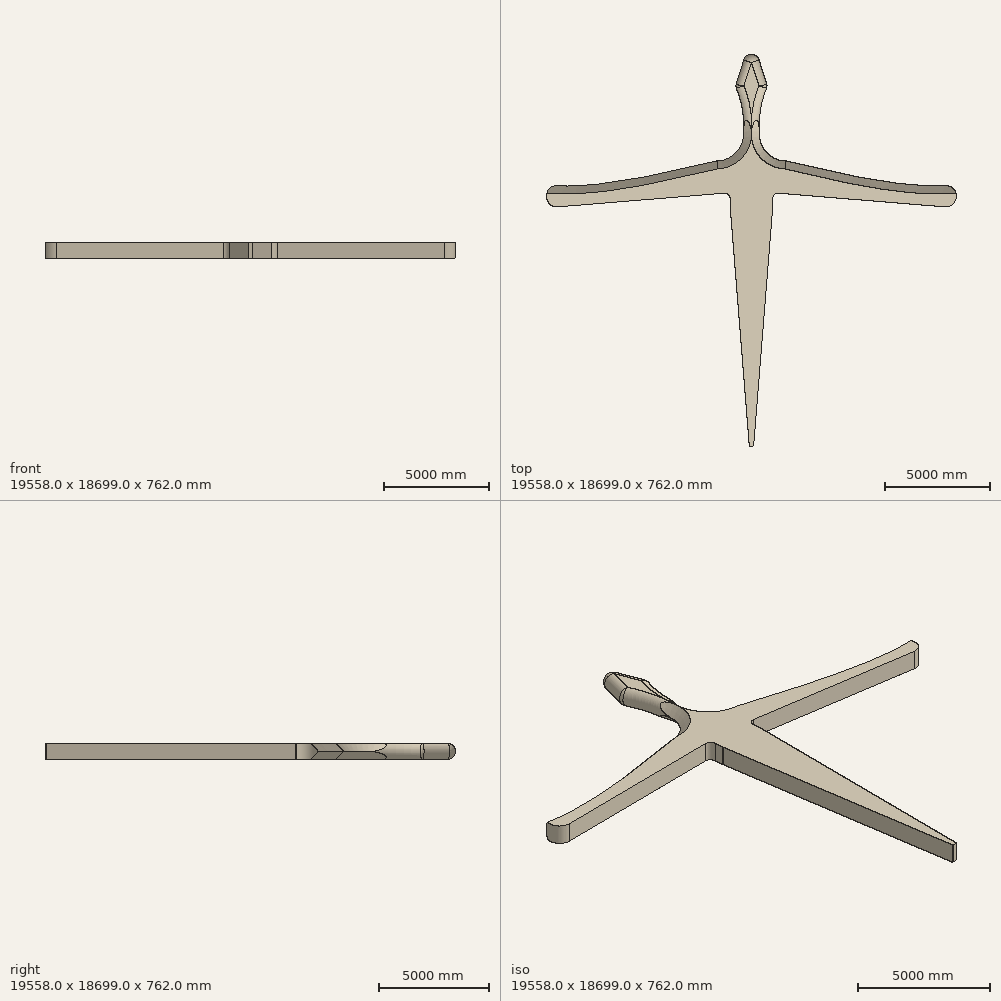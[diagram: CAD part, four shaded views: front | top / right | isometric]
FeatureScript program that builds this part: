
annotation { "Feature Type Name" : "Feature", "Feature Type Description" : "" }
export const myFeature = defineFeature(function(context is Context, id is Id, definition is map)
    precondition{}
    {
        {
            var Q0;
            Q0=qCreatedBy(makeId("Top.planeOp"),FACE);
            var sketch = newSketch(context, id + "F0", { "sketchPlane" : qUnion([Q0])});
            skArc(sketch, "E0", {"start": v(363.19, 1258.13) * mm, "mid": v(0, 1524) * mm, "end": v(-363.19, 1258.13) * mm});
            skLineSegment(sketch, "E1", {"start": v(-733.66, 89.4) * mm, "end": v(-363.19, 1258.13) * mm});
            skLineSegment(sketch, "E2", {"start": v(733.66, 89.4) * mm, "end": v(363.19, 1258.13) * mm});
            skPoint(sketch, "E3.end.orphan", {"position": v(0, 762) * mm});
            skArc(sketch, "E4", {"start": v(-381, -2286) * mm, "mid": v(-423.5, -1164.66) * mm, "end": v(-726.36, -84.15) * mm});
            skArc(sketch, "E5", {"start": v(726.36, -84.15) * mm, "mid": v(423.5, -1164.66) * mm, "end": v(381, -2286) * mm});
            skPoint(sketch, "E6.center.orphan", {"position": v(0, 0) * mm});
            skPoint(sketch, "E7.visualSharp", {"position": v(-762, 0) * mm});
            skArc(sketch, "E7.filletArc", {"start": v(-733.66, 89.4) * mm, "mid": v(-745.31, 1.98) * mm, "end": v(-726.36, -84.15) * mm});
            skPoint(sketch, "E8.visualSharp", {"position": v(762, 0) * mm});
            skArc(sketch, "E8.filletArc", {"start": v(726.36, -84.15) * mm, "mid": v(745.31, 1.98) * mm, "end": v(733.66, 89.4) * mm});
            skArc(sketch, "E9", {"start": v(-1651, -3556) * mm, "mid": v(-752.97, -3184.03) * mm, "end": v(-381, -2286) * mm});
            skArc(sketch, "E10", {"start": v(381, -2286) * mm, "mid": v(752.97, -3184.03) * mm, "end": v(1651, -3556) * mm});
            skFitSpline(sketch, "E11", {"points": [v(-1651, -3556) * mm, v(-9271, -4733.18) * mm, v(-11645.05, -3985.73) * mm], "startDerivative": vector(-13701.74, -3365.96) * mm, "endDerivative": vector(-5543.68, 3094.65) * mm});
            skFitSpline(sketch, "E12.MirrorCS", {"points": [v(1651, -3556) * mm, v(9271, -4733.18) * mm, v(11645.05, -3985.73) * mm], "startDerivative": vector(13701.74, -3365.96) * mm, "endDerivative": vector(5543.68, 3094.65) * mm});
            skArc(sketch, "E13", {"start": v(-9271, -4733.18) * mm, "mid": v(-9779, -5241.18) * mm, "end": v(-9271, -5749.18) * mm});
            skArc(sketch, "E14", {"start": v(9271, -5749.18) * mm, "mid": v(9779, -5241.18) * mm, "end": v(9271, -4733.18) * mm});
            skPoint(sketch, "E15.end.orphan", {"position": v(-9271, -5749.18) * mm});
            skLineSegment(sketch, "E16", {"start": v(-9271, -5749.18) * mm, "end": v(-1290.8, -5093.27) * mm});
            skLineSegment(sketch, "E17", {"start": v(9271, -5749.18) * mm, "end": v(1290.8, -5093.27) * mm});
            skLineSegment(sketch, "E18.bottom", {"start": v(-1016, -5749.18) * mm, "end": v(-1016, -5749.18) * mm});
            skLineSegment(sketch, "E18.top", {"start": v(-1016, -3806.69) * mm, "end": v(-1016, -3806.69) * mm});
            skLineSegment(sketch, "E18.left", {"start": v(-1016, -5749.18) * mm, "end": v(-1016, -5346.42) * mm});
            skLineSegment(sketch, "E18.right", {"start": v(-1016, -5739.04) * mm, "end": v(-1016, -5070.69) * mm});
            skLineSegment(sketch, "E19", {"start": v(1016, -5739.04) * mm, "end": v(1016, -5346.42) * mm});
            skPoint(sketch, "E20.visualSharp", {"position": v(-1016, -5070.69) * mm});
            skArc(sketch, "E20.filletArc", {"start": v(-1016, -5346.42) * mm, "mid": v(-1097.9, -5159.6) * mm, "end": v(-1290.8, -5093.27) * mm});
            skPoint(sketch, "E21.visualSharp", {"position": v(1016, -5070.69) * mm});
            skArc(sketch, "E21.filletArc", {"start": v(1290.8, -5093.27) * mm, "mid": v(1097.9, -5159.6) * mm, "end": v(1016, -5346.42) * mm});
            skLineSegment(sketch, "E22", {"start": v(-1015.2, -5759.3) * mm, "end": v(-103.92, -17150.16) * mm});
            skLineSegment(sketch, "E23", {"start": v(103.87, -17150.76) * mm, "end": v(1015.2, -5759.3) * mm});
            skPoint(sketch, "E24.visualSharp", {"position": v(-1016, -5749.18) * mm});
            skArc(sketch, "E24.filletArc", {"start": v(-1016, -5739.04) * mm, "mid": v(-1015.8, -5749.17) * mm, "end": v(-1015.2, -5759.3) * mm});
            skPoint(sketch, "E25.visualSharp", {"position": v(1016, -5749.18) * mm});
            skArc(sketch, "E25.filletArc", {"start": v(1015.2, -5759.3) * mm, "mid": v(1015.8, -5749.17) * mm, "end": v(1016, -5739.04) * mm});
            skLineSegment(sketch, "E26", {"start": v(72.12, -17174.4) * mm, "end": v(-77.67, -17174.4) * mm});
            skPoint(sketch, "E27.visualSharp", {"position": v(101.98, -17174.4) * mm});
            skArc(sketch, "E27.filletArc", {"start": v(72.12, -17174.4) * mm, "mid": v(93.35, -17169.77) * mm, "end": v(103.87, -17150.76) * mm});
            skPoint(sketch, "E28.visualSharp", {"position": v(-101.98, -17174.4) * mm});
            skArc(sketch, "E28.filletArc", {"start": v(-103.92, -17150.16) * mm, "mid": v(-95.53, -17167.41) * mm, "end": v(-77.67, -17174.4) * mm});
            skLineSegment(sketch, "E29.0", {"start": v(491.53, 12.65) * mm, "end": v(121.06, 1181.38) * mm});
            skArc(sketch, "E29.1", {"start": v(121.06, 1181.38) * mm, "mid": v(0, 1270) * mm, "end": v(-121.06, 1181.38) * mm});
            skLineSegment(sketch, "E29.2", {"start": v(-491.53, 12.65) * mm, "end": v(-121.06, 1181.38) * mm});
            skArc(sketch, "E30", {"start": v(-491.53, 12.65) * mm, "mid": v(0, -491.7) * mm, "end": v(491.53, 12.65) * mm});
            skSolve(sketch);
        }
        {
            var Q0;
            Q0=makeQuery(id+"F0.imprint","IMPRINT",FACE,{"disambiguationData":[TD([[makeQuery(id+"F0.imprint","IMPRINT",EDGE,{"derivedFrom":sQuery(id+"F0.wireOp",EDGE,"E0")}),1.0]])]});
            var Q1;
            Q1=makeQuery(id+"F0.imprint","IMPRINT",FACE,{"disambiguationData":[TD([[makeQuery(id+"F0.imprint","IMPRINT",EDGE,{"derivedFrom":sQuery(id+"F0.wireOp",EDGE,"E29.0")}),1.0]])]});
            extrude(context, id + "F1", {"entities" : qUnion([Q0, Q1]), "depth" : 762 * mm});
        }
        {
            var Q0;
            Q0=makeQuery(id+"F1.opExtrude","CAP_EDGE",EDGE,{"disambiguationData":[OSD([sQuery(id+"F0.wireOp",EDGE,"E11")])],"isStart":false});
            var Q1;
            Q1=makeQuery(id+"F1.opExtrude","CAP_EDGE",EDGE,{"disambiguationData":[OSD([sQuery(id+"F0.wireOp",EDGE,"E12.MirrorCS")])],"isStart":false});
            var Q2;
            Q2=makeQuery(id+"F1.opExtrude","CAP_EDGE",EDGE,{"disambiguationData":[OSD([sQuery(id+"F0.wireOp",EDGE,"E10")])],"isStart":false});
            var Q3;
            Q3=makeQuery(id+"F1.opExtrude","CAP_EDGE",EDGE,{"disambiguationData":[OSD([sQuery(id+"F0.wireOp",EDGE,"E9")])],"isStart":false});
            var Q4;
            Q4=makeQuery(id+"F1.opExtrude","CAP_EDGE",EDGE,{"disambiguationData":[OSD([sQuery(id+"F0.wireOp",EDGE,"E12.MirrorCS")])],"isStart":true});
            var Q5;
            Q5=makeQuery(id+"F1.opExtrude","CAP_EDGE",EDGE,{"disambiguationData":[OSD([sQuery(id+"F0.wireOp",EDGE,"E11")])],"isStart":true});
            var Q6;
            Q6=makeQuery(id+"F1.opExtrude","CAP_EDGE",EDGE,{"disambiguationData":[OSD([sQuery(id+"F0.wireOp",EDGE,"E10")])],"isStart":true});
            var Q7;
            Q7=makeQuery(id+"F1.opExtrude","CAP_EDGE",EDGE,{"disambiguationData":[OSD([sQuery(id+"F0.wireOp",EDGE,"E9")])],"isStart":true});
            chamfer(context, id + "F2", {"entities" : qUnion([Q0, Q1, Q2, Q3, Q4, Q5, Q6, Q7]), "width" : 381 * mm, "tangentPropagation" : true});
        }
        {
            var Q0;
            Q0=makeQuery(id+"F1.opExtrude","CAP_EDGE",EDGE,{"disambiguationData":[OSD([sQuery(id+"F0.wireOp",EDGE,"E0")])],"isStart":false});
            var Q1;
            Q1=makeQuery(id+"F1.opExtrude","CAP_EDGE",EDGE,{"disambiguationData":[OSD([sQuery(id+"F0.wireOp",EDGE,"E0")])],"isStart":true});
            fillet(context, id + "F3", {"entities" : qUnion([Q0, Q1]), "radius" : 381 * mm, "tangentPropagation" : true, "allowEdgeOverflow" : false});
        }
    });
